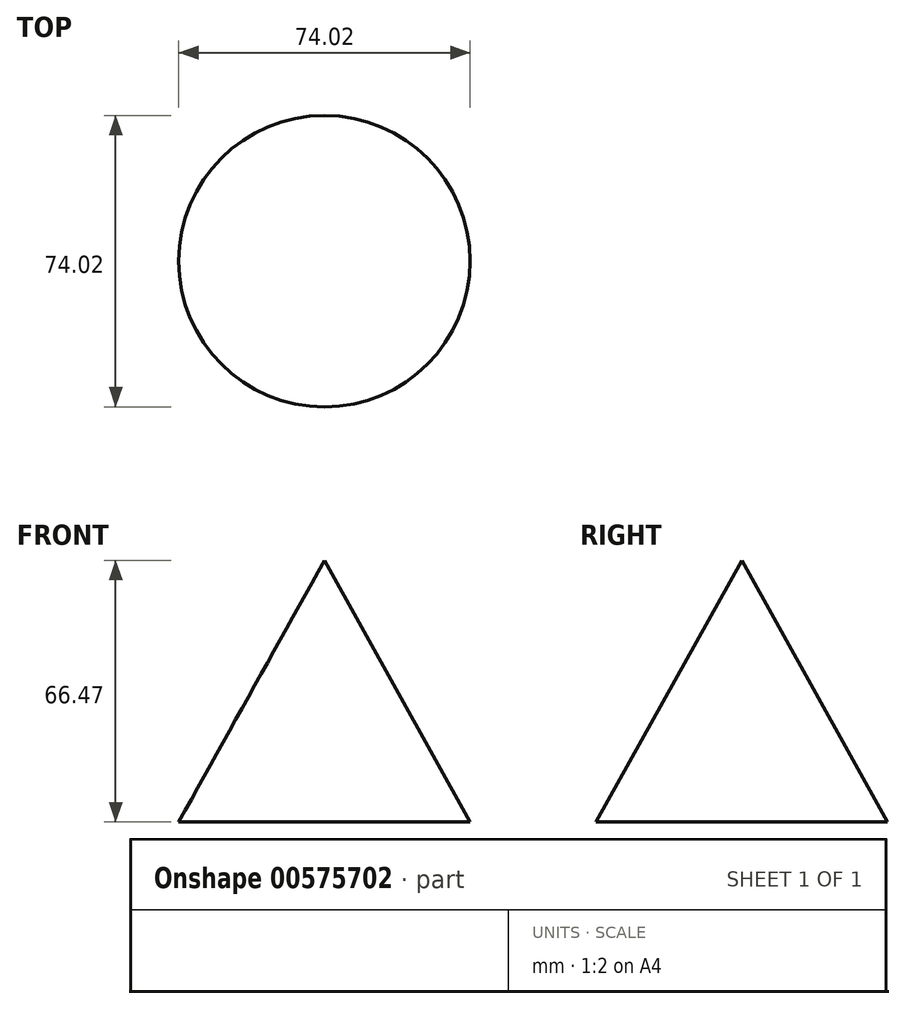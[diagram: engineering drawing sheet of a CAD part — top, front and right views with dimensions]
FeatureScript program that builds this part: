
annotation { "Feature Type Name" : "Feature", "Feature Type Description" : "" }
export const myFeature = defineFeature(function(context is Context, id is Id, definition is map)
    precondition{}
    {
        {
            var Q0;
            Q0=qCreatedBy(makeId("Front.planeOp"),FACE);
            var sketch = newSketch(context, id + "F0", { "sketchPlane" : qUnion([Q0])});
            skLineSegment(sketch, "E0", {"start": v(0, 66.47) * mm, "end": v(-37.01, 0) * mm});
            skLineSegment(sketch, "E1", {"start": v(-37.01, 0) * mm, "end": v(0, 0) * mm});
            skLineSegment(sketch, "E2", {"start": v(0, 66.47) * mm, "end": v(0, 0) * mm});
            skSolve(sketch);
        }
        {
            var Q0;
            Q0 = qSketchRegion(id + "F0", true);
            var Q1;
            Q1=sQuery(id+"F0.wireOp",EDGE,"E2");
            revolve(context, id + "F1", {"entities" : qUnion([Q0]), "axis" : qUnion([Q1]), "revolveType" : RevolveType.FULL});
        }
    });
